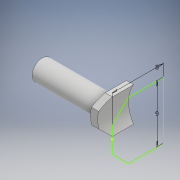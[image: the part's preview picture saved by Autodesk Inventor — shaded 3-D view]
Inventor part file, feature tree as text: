
AUTODESK INVENTOR PART (.ipt)
format: ipt  version: 2018 (Build 220112000, 112)  size: 180,736 bytes
history: native  units: mm
features: sketch x8, extrude x7, projected_geometry x1
ambient origin geometry x8: Origin, YZ Plane, XZ Plane, XY Plane, X Axis, Y Axis, Z Axis, Center Point
bodies: Solid1 (feature_tree)
feature tree (16):
  extrude  "Extrusion1"  Depth=10.0mm TaperAngle=0.0deg
  sketch  "Sketch2"  dims[d3=9.0mm d4=8.0mm d5=10.0mm d6=0.0mm]
  extrude  "Extrusion2"  Depth=10.0mm TaperAngle=0.0deg
  extrude  "Extrusion3"  Depth=1.125mm
  extrude  "Extrusion4"  Depth=1.6mm
  extrude  "Extrusion5"  Depth=1.8mm
  extrude  "Extrusion6"  Depth=2.4mm
  extrude  "Extrusion7"  Depth=3.32mm
  sketch  "Sketch1"  dims[d0=10.0mm d1=10.0mm d2=0.0mm]
  sketch  "Sketch3"  dims[d9=1.125mm d10=1.125mm]
  sketch  "Sketch4"  dims[d12=0.0mm d13=0.0mm d16=1.6mm]
  sketch  "Sketch5"  dims[d18=1.6mm d21=1.8mm]
  projected_geometry  "Projected Loop1"
  sketch  "Sketch6"  dims[d23=1.8mm d24=2.4mm]
  sketch  "Sketch7"  dims[d26=3.32mm d27=3.32mm]
  sketch  "Sketch8"  dims[d29=10.0mm d30=0.0mm d31=3.15mm d32=2.4mm d33=15.0mm d34=0.0mm d35=15.0mm d36=0.0mm d37=1.075mm d38=10.0mm d39=0.0mm]
